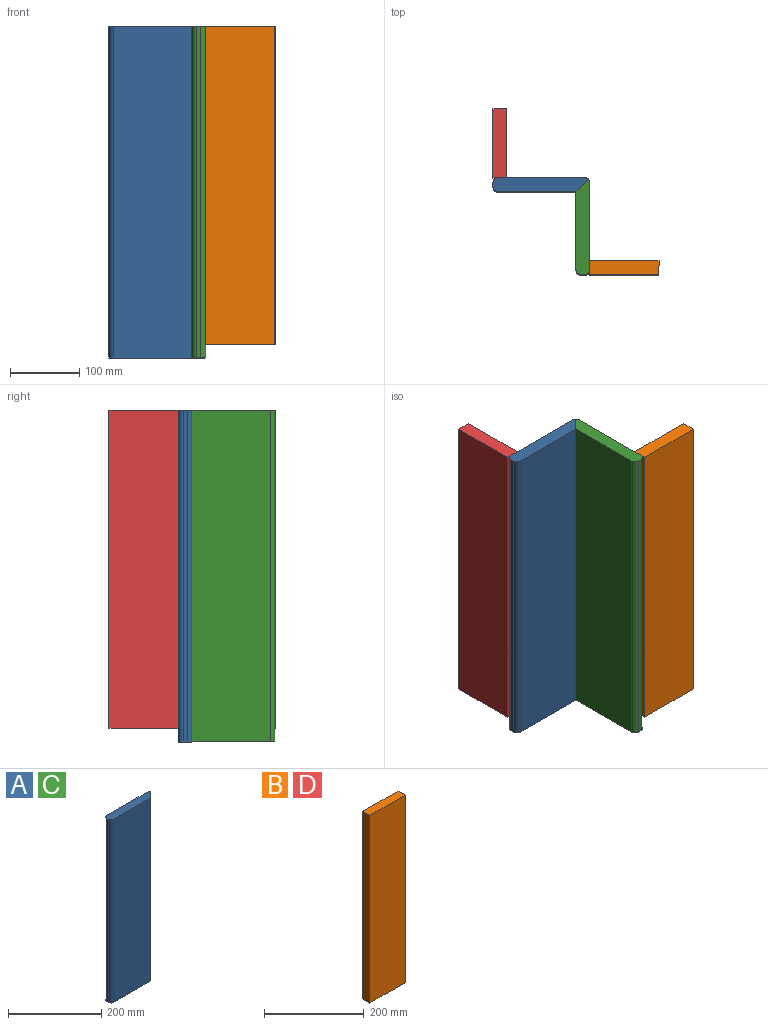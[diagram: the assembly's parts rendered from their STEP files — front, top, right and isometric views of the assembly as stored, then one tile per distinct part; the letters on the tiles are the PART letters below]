
ASSEMBLY  parts=4 mates=2
PART A: 9 faces, bbox 137.9x20x480 mm
  f0: plane 480x6mm, normal (-1,0,0), area 2880mm2, adj f3,f4,f5,f7
  f1: plane 480x113mm, normal (0,-1,0), area 54240mm2, adj f3,f4,f5,f8
  f2: plane 480x126mm, normal (0,1,0), area 60480mm2, adj f3,f4,f6,f7
  f3: plane 137.95x20mm, normal (0,0,1), area 2573.7mm2, adj f0,f1,f2,f5,f6,f7,f8
  f4: plane 137.95x20mm, normal (0,0,-1), area 2573.7mm2, adj f0,f1,f2,f5,f6,f7,f8
  f5: cylinder r=7mm len=480mm, axis (0,0,1), area 5277.9mm2, adj f0,f1,f3,f4
  f6: cylinder r=7mm len=480mm, axis (0,0,1), area 2638.9mm2, adj f2,f3,f4,f8
  f7: cylinder r=7mm len=480mm, axis (0,0,-1), area 5277.9mm2, adj f0,f2,f3,f4
  f8: plane 480x17.95mm, normal (0.71,-0.71,0), area 12184.7mm2, adj f1,f3,f4,f6
PART B: 6 faces, bbox 100x20x460 mm
  f0: plane 460x20mm, normal (-1,0,0), area 9200mm2, adj f1,f3,f4,f5
  f1: plane 460x100mm, normal (0,-1,0), area 46000mm2, adj f0,f2,f4,f5
  f2: plane 460x20mm, normal (1,0,0), area 9200mm2, adj f1,f3,f4,f5
  f3: plane 460x100mm, normal (0,1,0), area 46000mm2, adj f0,f2,f4,f5
  f4: plane 100x20mm, normal (0,0,1), area 2000mm2, adj f0,f1,f2,f3
  f5: plane 100x20mm, normal (0,0,-1), area 2000mm2, adj f0,f1,f2,f3
PART C: same geometry as A
PART D: same geometry as B
PLACE A t=(-1.86,287.12,-74.81)mm
PLACE B rot(axis=(0,-1,0),180deg) t=(238.14,167.11,405.19)mm
PLACE C rot(axis=(0.71,0.71,0),180deg) t=(118.14,167.12,405.19)mm
PLACE D rot(axis=(0,0,-1),90deg) t=(-1.86,407.12,-54.81)mm
MATE planar C.f8 <-> A.f8  axis (-0.71,0.71,0) through (127.12,296.09,165.19)mm
MATE planar D.f2 <-> A.f2  axis (0,-1,0) through (8.14,307.12,175.19)mm
